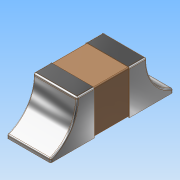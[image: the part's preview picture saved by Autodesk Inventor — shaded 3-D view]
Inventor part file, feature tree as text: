
AUTODESK INVENTOR PART (.ipt)
format: ipt  version: 2016 (Build 200138000, 138)  size: 192,000 bytes
history: native  units: mm
features: extrude x3, fillet x3, sketch x2, mirror x1, projected_geometry x1
ambient origin geometry x8: Origin, YZ Plane, XZ Plane, XY Plane, X Axis, Y Axis, Z Axis, Center Point
bodies: Body1 (feature_tree)
feature tree (10):
  extrude  "Extrusion4"  Depth=1.225mm
  sketch  "Sketch11"  dims[d9=1.225mm d10=0.0mm d11=1.25mm d12=0.5mm d13=0.0mm d14=0.1mm d15=1.25mm d16=0.0mm d17=1.15mm d18=0.0425mm d19=0.03mm]
  extrude  "Extrusion5"  Depth=1.25mm
  extrude  "Extrusion6"  Depth=0.5mm TaperAngle=0.0deg
  fillet  "Fillet1"  Radius=0.1mm
  fillet  "Fillet2"  Radius=1.25mm
  mirror  "Mirror1"
  fillet  "Fillet3"  Radius=1.15mm
  sketch  "Sketch10"  dims[d7=1.0mm d8=1.225mm]
  projected_geometry  "Projected Loop1"
